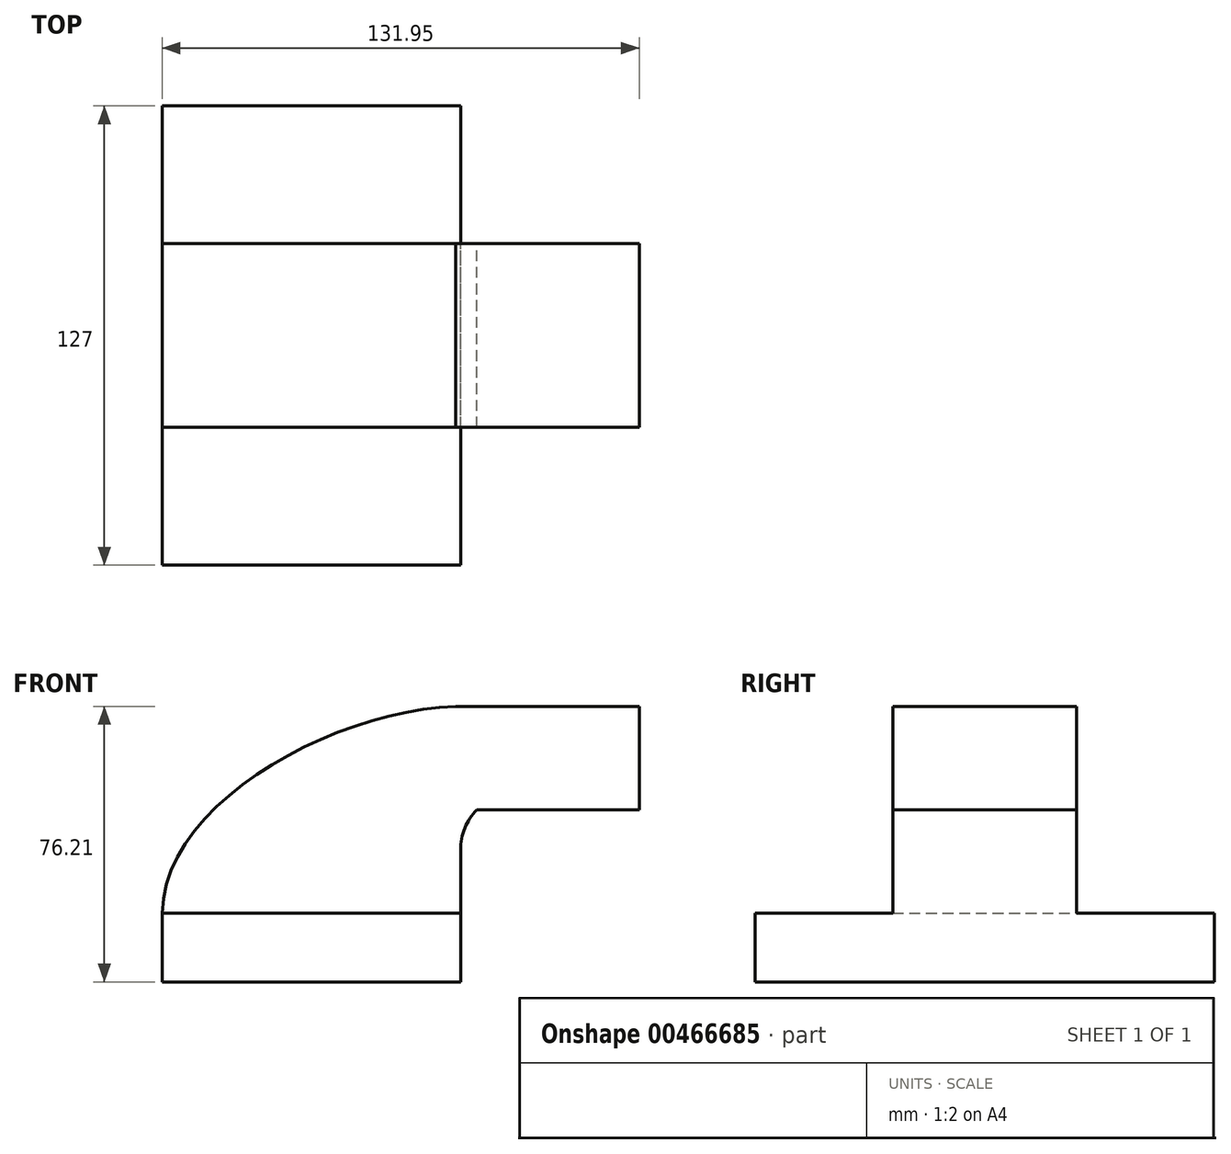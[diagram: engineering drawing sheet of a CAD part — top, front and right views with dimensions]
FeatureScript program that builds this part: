
annotation { "Feature Type Name" : "Feature", "Feature Type Description" : "" }
export const myFeature = defineFeature(function(context is Context, id is Id, definition is map)
    precondition{}
    {
        {
            var Q0;
            Q0=qCreatedBy(makeId("Front.planeOp"),FACE);
            var sketch = newSketch(context, id + "F0", { "sketchPlane" : qUnion([Q0])});
            skLineSegment(sketch, "E0.bottom", {"start": v(-41.28, 9.52) * mm, "end": v(41.28, 9.52) * mm});
            skLineSegment(sketch, "E0.top", {"start": v(-41.27, -9.53) * mm, "end": v(41.27, -9.53) * mm});
            skLineSegment(sketch, "E0.left", {"start": v(-41.28, 9.52) * mm, "end": v(-41.28, -9.53) * mm});
            skLineSegment(sketch, "E0.right", {"start": v(41.27, 9.52) * mm, "end": v(41.27, -9.52) * mm});
            skPoint(sketch, "E0.middle", {"position": v(0, 0) * mm});
            skLineSegment(sketch, "E1.bottom", {"start": v(90.67, 38.1) * mm, "end": v(39.87, 38.1) * mm});
            skLineSegment(sketch, "E1.top", {"start": v(90.67, 66.67) * mm, "end": v(39.87, 66.67) * mm});
            skLineSegment(sketch, "E1.left", {"start": v(90.67, 38.1) * mm, "end": v(90.67, 66.67) * mm});
            skLineSegment(sketch, "E1.right", {"start": v(39.87, 38.1) * mm, "end": v(39.87, 66.67) * mm});
            skPoint(sketch, "E1.middle", {"position": v(65.27, 52.39) * mm});
            skLineSegment(sketch, "E2", {"start": v(41.27, 9.52) * mm, "end": v(41.27, 27) * mm});
            skArc(sketch, "E3", {"start": v(41.27, 27) * mm, "mid": v(45.92, 38.23) * mm, "end": v(57.15, 42.88) * mm});
            skLineSegment(sketch, "E4", {"start": v(57.15, 42.88) * mm, "end": v(85.72, 42.88) * mm});
            skLineSegment(sketch, "E5.0", {"start": v(57.15, 61.93) * mm, "end": v(85.72, 61.93) * mm});
            skArc(sketch, "E5.1", {"start": v(22.22, 27) * mm, "mid": v(32.45, 51.7) * mm, "end": v(57.15, 61.93) * mm});
            skLineSegment(sketch, "E5.2", {"start": v(22.22, 9.52) * mm, "end": v(22.22, 27) * mm});
            skLineSegment(sketch, "E6", {"start": v(85.72, 42.88) * mm, "end": v(85.72, 61.93) * mm});
            skFitSpline(sketch, "E7", {"points": [v(-41.28, 9.53) * mm, v(39.87, 66.68) * mm], "startDerivative": vector(1.9, 92.6) * mm, "endDerivative": vector(100.05, 3.58) * mm});
            skSolve(sketch);
        }
        {
            var Q0;
            Q0=makeQuery(id+"F0.imprint","IMPRINT",FACE,{"disambiguationData":[TD([[makeQuery(id+"F0.imprint","IMPRINT",EDGE,{"derivedFrom":sQuery(id+"F0.wireOp",EDGE,"E0.top")}),1.0]])]});
            extrude(context, id + "F1", {"entities" : qUnion([Q0]), "depth" : 127 * mm, "symmetric" : true});
        }
        {
            var Q0;
            Q0 = qSketchRegion(id + "F0", true);
            extrude(context, id + "F2", {"entities" : qUnion([Q0]), "operationType" : NewBodyOperationType.ADD, "depth" : 50.8 * mm, "symmetric" : true});
        }
    });
